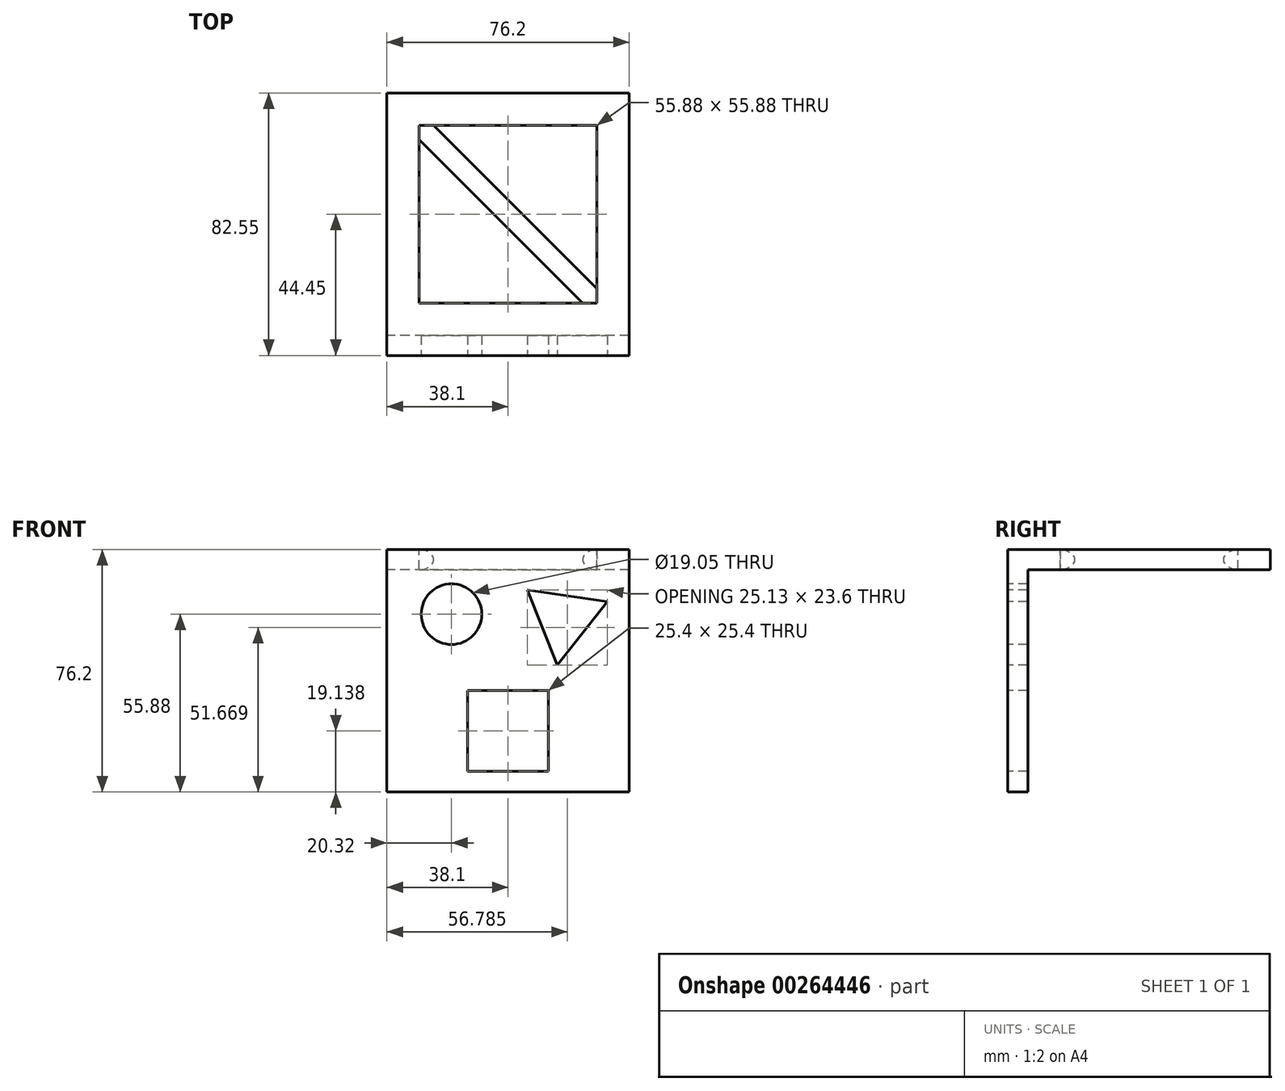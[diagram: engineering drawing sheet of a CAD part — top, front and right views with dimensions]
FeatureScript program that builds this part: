
annotation { "Feature Type Name" : "Feature", "Feature Type Description" : "" }
export const myFeature = defineFeature(function(context is Context, id is Id, definition is map)
    precondition{}
    {
        {
            var Q0;
            Q0=qCreatedBy(makeId("Front.planeOp"),FACE);
            var sketch = newSketch(context, id + "F0", { "sketchPlane" : qUnion([Q0])});
            skLineSegment(sketch, "E0.bottom", {"start": v(38.1, -38.1) * mm, "end": v(-38.1, -38.1) * mm});
            skLineSegment(sketch, "E0.top", {"start": v(38.1, 38.1) * mm, "end": v(-38.1, 38.1) * mm});
            skLineSegment(sketch, "E0.left", {"start": v(38.1, -38.1) * mm, "end": v(38.1, 38.1) * mm});
            skLineSegment(sketch, "E0.right", {"start": v(-38.1, -38.1) * mm, "end": v(-38.1, 38.1) * mm});
            skPoint(sketch, "E0.middle", {"position": v(0, 0) * mm});
            skCircle(sketch, "E1", {"center": v(-17.78, 17.78) * mm, "radius": 9.53 * mm});
            skLineSegment(sketch, "E2", {"start": v(6.12, 25.37) * mm, "end": v(15.51, 1.77) * mm});
            skLineSegment(sketch, "E3", {"start": v(15.51, 1.77) * mm, "end": v(31.25, 21.7) * mm});
            skLineSegment(sketch, "E4", {"start": v(6.12, 25.37) * mm, "end": v(31.25, 21.7) * mm});
            skLineSegment(sketch, "E5", {"start": v(-17.78, 17.78) * mm, "end": v(-17.78, 38.1) * mm, "construction": true});
            skLineSegment(sketch, "E6.bottom", {"start": v(12.7, -31.66) * mm, "end": v(-12.7, -31.66) * mm});
            skLineSegment(sketch, "E6.top", {"start": v(12.7, -6.26) * mm, "end": v(-12.7, -6.26) * mm});
            skLineSegment(sketch, "E6.left", {"start": v(12.7, -31.66) * mm, "end": v(12.7, -6.26) * mm});
            skLineSegment(sketch, "E6.right", {"start": v(-12.7, -31.66) * mm, "end": v(-12.7, -6.26) * mm});
            skPoint(sketch, "E6.middle", {"position": v(0, -18.96) * mm});
            skSolve(sketch);
        }
        {
            var Q0;
            Q0=makeQuery(id+"F0.imprint","IMPRINT",FACE,{"disambiguationData":[TD([[makeQuery(id+"F0.imprint","IMPRINT",EDGE,{"derivedFrom":sQuery(id+"F0.wireOp",EDGE,"E0.bottom")}),-1.0]])]});
            extrude(context, id + "F1", {"entities" : qUnion([Q0]), "oppositeDirection" : true, "depth" : 6.35 * mm});
        }
        {
            var Q0;
            Q0=makeQuery(id+"F1.opExtrude","SWEPT_FACE",FACE,{"disambiguationData":[OSD([sQuery(id+"F0.wireOp",EDGE,"E0.top")])]});
            var sketch = newSketch(context, id + "F2", { "sketchPlane" : qUnion([Q0])});
            skLineSegment(sketch, "E7.bottom", {"start": v(-38.1, 6.35) * mm, "end": v(38.1, 6.35) * mm});
            skLineSegment(sketch, "E7.top", {"start": v(-38.1, 82.55) * mm, "end": v(38.1, 82.55) * mm});
            skLineSegment(sketch, "E7.left", {"start": v(-38.1, 6.35) * mm, "end": v(-38.1, 82.55) * mm});
            skLineSegment(sketch, "E7.right", {"start": v(38.1, 6.35) * mm, "end": v(38.1, 82.55) * mm});
            skLineSegment(sketch, "E8.bottom", {"start": v(-27.94, 72.39) * mm, "end": v(27.94, 72.39) * mm});
            skLineSegment(sketch, "E8.top", {"start": v(-27.94, 16.51) * mm, "end": v(27.94, 16.51) * mm});
            skLineSegment(sketch, "E8.left", {"start": v(-27.94, 72.39) * mm, "end": v(-27.94, 16.51) * mm});
            skLineSegment(sketch, "E8.right", {"start": v(27.94, 72.39) * mm, "end": v(27.94, 16.51) * mm});
            skLineSegment(sketch, "E9", {"start": v(-27.94, 67.9) * mm, "end": v(23.45, 16.5) * mm});
            skLineSegment(sketch, "E10", {"start": v(-23.45, 72.39) * mm, "end": v(27.94, 21) * mm});
            skSolve(sketch);
        }
        {
            var Q0;
            Q0 = qSketchRegion(id + "F2", true);
            extrude(context, id + "F3", {"entities" : qUnion([Q0]), "operationType" : NewBodyOperationType.ADD, "oppositeDirection" : true, "depth" : 6.35 * mm});
        }
        {
            var Q0;
            {var subQ7=sQuery(id+"F2.wireOp",EDGE,"E9");Q0=makeQuery(id+"F2.imprint","IMPRINT",FACE,{"disambiguationData":[TD([[makeQuery(id+"F2.imprint","IMPRINT",EDGE,{"derivedFrom":subQ7}),1.0]])]});}
            extrude(context, id + "F4", {"entities" : qUnion([Q0]), "operationType" : NewBodyOperationType.ADD, "oppositeDirection" : true, "depth" : 6.35 * mm});
        }
        {
            var Q0;
            Q0=makeQuery(id+"F4.opExtrude","CAP_EDGE",EDGE,{"disambiguationData":[OSD([sQuery(id+"F2.wireOp",EDGE,"E10")])],"isStart":true});
            var Q1;
            Q1=makeQuery(id+"F4.opExtrude","CAP_EDGE",EDGE,{"disambiguationData":[OSD([sQuery(id+"F2.wireOp",EDGE,"E9")])],"isStart":true});
            var Q2;
            Q2=makeQuery(id+"F4.opExtrude","CAP_EDGE",EDGE,{"disambiguationData":[OSD([sQuery(id+"F2.wireOp",EDGE,"E9")])],"isStart":false});
            var Q3;
            Q3=makeQuery(id+"F4.opExtrude","CAP_EDGE",EDGE,{"disambiguationData":[OSD([sQuery(id+"F2.wireOp",EDGE,"E10")])],"isStart":false});
            fillet(context, id + "F5", {"entities" : qUnion([Q0, Q1, Q2, Q3]), "radius" : 3.17 * mm, "tangentPropagation" : true, "allowEdgeOverflow" : false});
        }
    });
